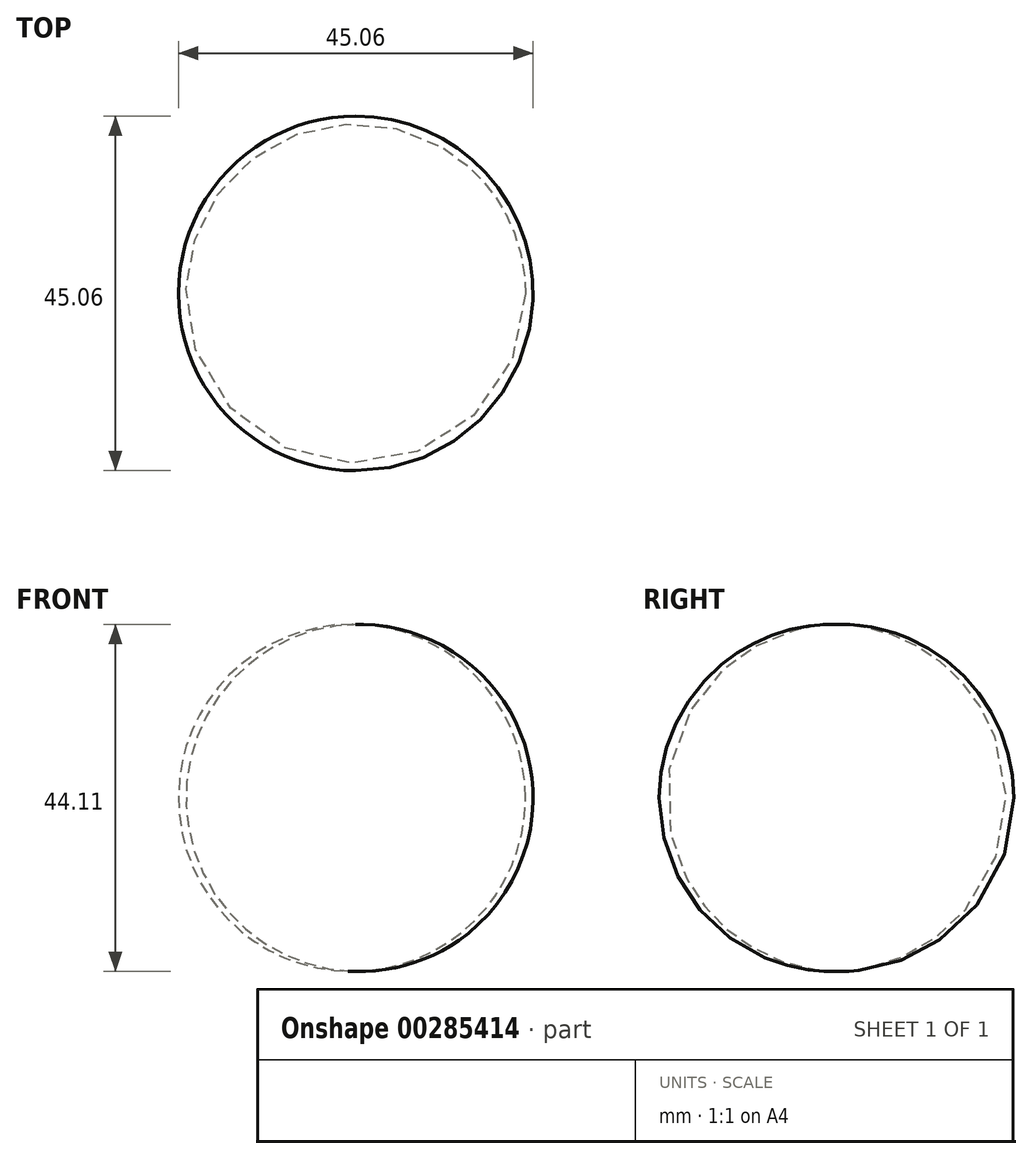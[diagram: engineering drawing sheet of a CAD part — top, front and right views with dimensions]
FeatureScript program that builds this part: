
annotation { "Feature Type Name" : "Feature", "Feature Type Description" : "" }
export const myFeature = defineFeature(function(context is Context, id is Id, definition is map)
    precondition{}
    {
        {
            var Q0;
            Q0=qCreatedBy(makeId("Front.planeOp"),FACE);
            var sketch = newSketch(context, id + "F0", { "sketchPlane" : qUnion([Q0])});
            skArc(sketch, "E0", {"start": v(-45.45, 52.6) * mm, "mid": v(-67.48, 31.04) * mm, "end": v(-46.41, 8.53) * mm});
            skLineSegment(sketch, "E1", {"start": v(-46.41, 8.53) * mm, "end": v(-45.45, 52.6) * mm});
            skSolve(sketch);
        }
        {
            var Q0;
            Q0=qSketchRegion(id+"F0",true);
            var Q1;
            Q1=sQuery(id+"F0.wireOp",EDGE,"E1");
            revolve(context, id + "F1", {"entities" : qUnion([Q0]), "axis" : qUnion([Q1]), "revolveType" : RevolveType.FULL});
        }
    });
